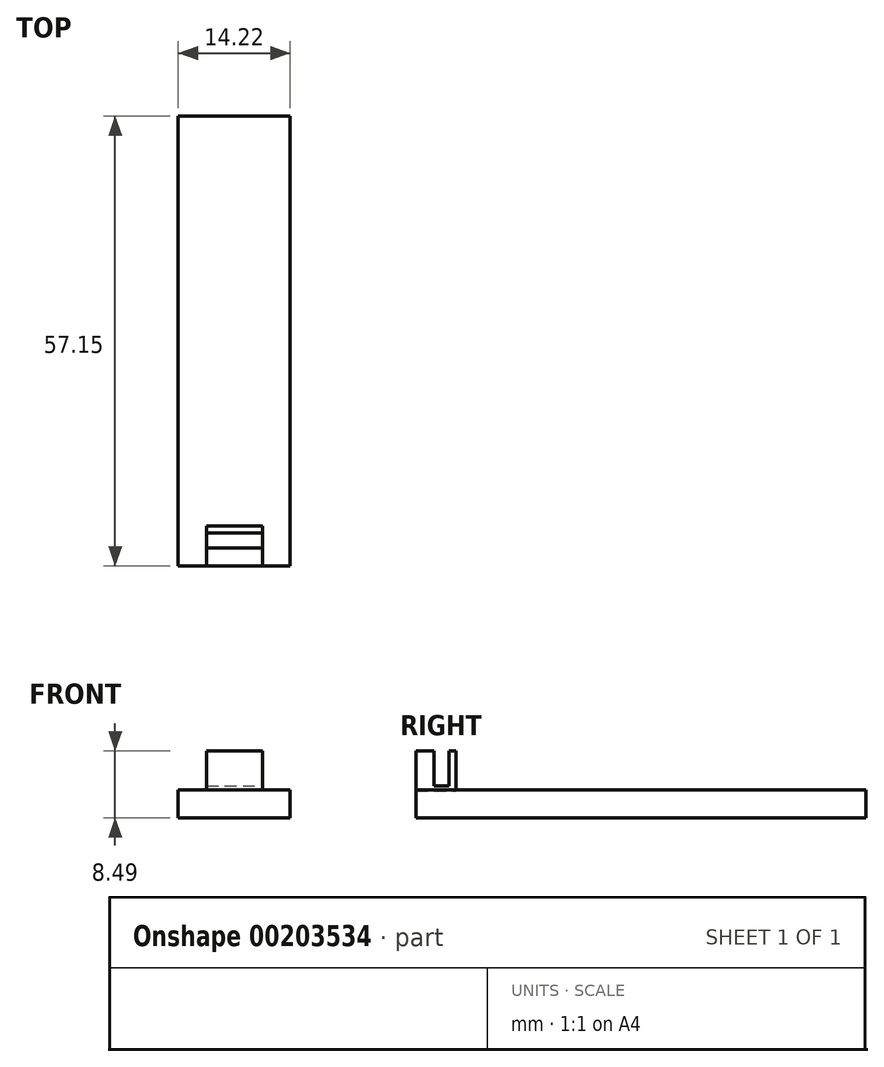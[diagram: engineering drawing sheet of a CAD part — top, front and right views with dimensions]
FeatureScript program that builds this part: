
annotation { "Feature Type Name" : "Feature", "Feature Type Description" : "" }
export const myFeature = defineFeature(function(context is Context, id is Id, definition is map)
    precondition{}
    {
        {
            var Q0;
            Q0=qCreatedBy(makeId("Front.planeOp"),FACE);
            var sketch = newSketch(context, id + "F0", { "sketchPlane" : qUnion([Q0])});
            skLineSegment(sketch, "E0.bottom", {"start": v(-7.17, 1.82) * mm, "end": v(7.05, 1.82) * mm});
            skLineSegment(sketch, "E0.top", {"start": v(-7.17, -1.73) * mm, "end": v(7.05, -1.73) * mm});
            skLineSegment(sketch, "E0.left", {"start": v(-7.17, 1.82) * mm, "end": v(-7.17, -1.73) * mm});
            skLineSegment(sketch, "E0.right", {"start": v(7.05, 1.82) * mm, "end": v(7.05, -1.73) * mm});
            skSolve(sketch);
        }
        {
            var Q0;
            Q0 = qSketchRegion(id + "F0", true);
            extrude(context, id + "F1", {"entities" : qUnion([Q0]), "depth" : 25.4 * mm, "hasSecondDirection" : true, "secondDirectionOppositeDirection" : true, "secondDirectionDepth" : 31.75 * mm});
        }
        {
            var Q0;
            Q0=qCreatedBy(makeId("Right.planeOp"),FACE);
            var sketch = newSketch(context, id + "F2", { "sketchPlane" : qUnion([Q0])});
            skLineSegment(sketch, "E1.bottom", {"start": v(-25.4, 6.76) * mm, "end": v(-20.32, 6.76) * mm});
            skLineSegment(sketch, "E1.top", {"start": v(-25.4, 1.68) * mm, "end": v(-20.32, 1.68) * mm});
            skLineSegment(sketch, "E1.left", {"start": v(-25.4, 6.76) * mm, "end": v(-25.4, 1.68) * mm});
            skLineSegment(sketch, "E1.right", {"start": v(-20.32, 6.76) * mm, "end": v(-20.32, 1.68) * mm});
            skSolve(sketch);
        }
        {
            var Q0;
            Q0 = qSketchRegion(id + "F2", true);
            extrude(context, id + "F3", {"entities" : qUnion([Q0]), "depth" : 3.56 * mm, "hasSecondDirection" : true, "secondDirectionOppositeDirection" : true, "secondDirectionDepth" : 3.56 * mm});
        }
        {
            var Q0;
            Q0=qCreatedBy(makeId("Right.planeOp"),FACE);
            var sketch = newSketch(context, id + "F4", { "sketchPlane" : qUnion([Q0])});
            skLineSegment(sketch, "E2.bottom", {"start": v(-23.13, 6.91) * mm, "end": v(-21.23, 6.91) * mm});
            skLineSegment(sketch, "E2.top", {"start": v(-23.13, 2.34) * mm, "end": v(-21.23, 2.34) * mm});
            skLineSegment(sketch, "E2.left", {"start": v(-23.13, 6.91) * mm, "end": v(-23.13, 2.34) * mm});
            skLineSegment(sketch, "E2.right", {"start": v(-21.23, 6.91) * mm, "end": v(-21.23, 2.34) * mm});
            skSolve(sketch);
        }
        {
            var Q0;
            Q0 = qSketchRegion(id + "F4", true);
            extrude(context, id + "F5", {"entities" : qUnion([Q0]), "operationType" : NewBodyOperationType.REMOVE, "oppositeDirection" : true, "depth" : 3.8 * mm, "hasSecondDirection" : true, "secondDirectionOppositeDirection" : false, "secondDirectionDepth" : 3.8 * mm});
        }
    });
